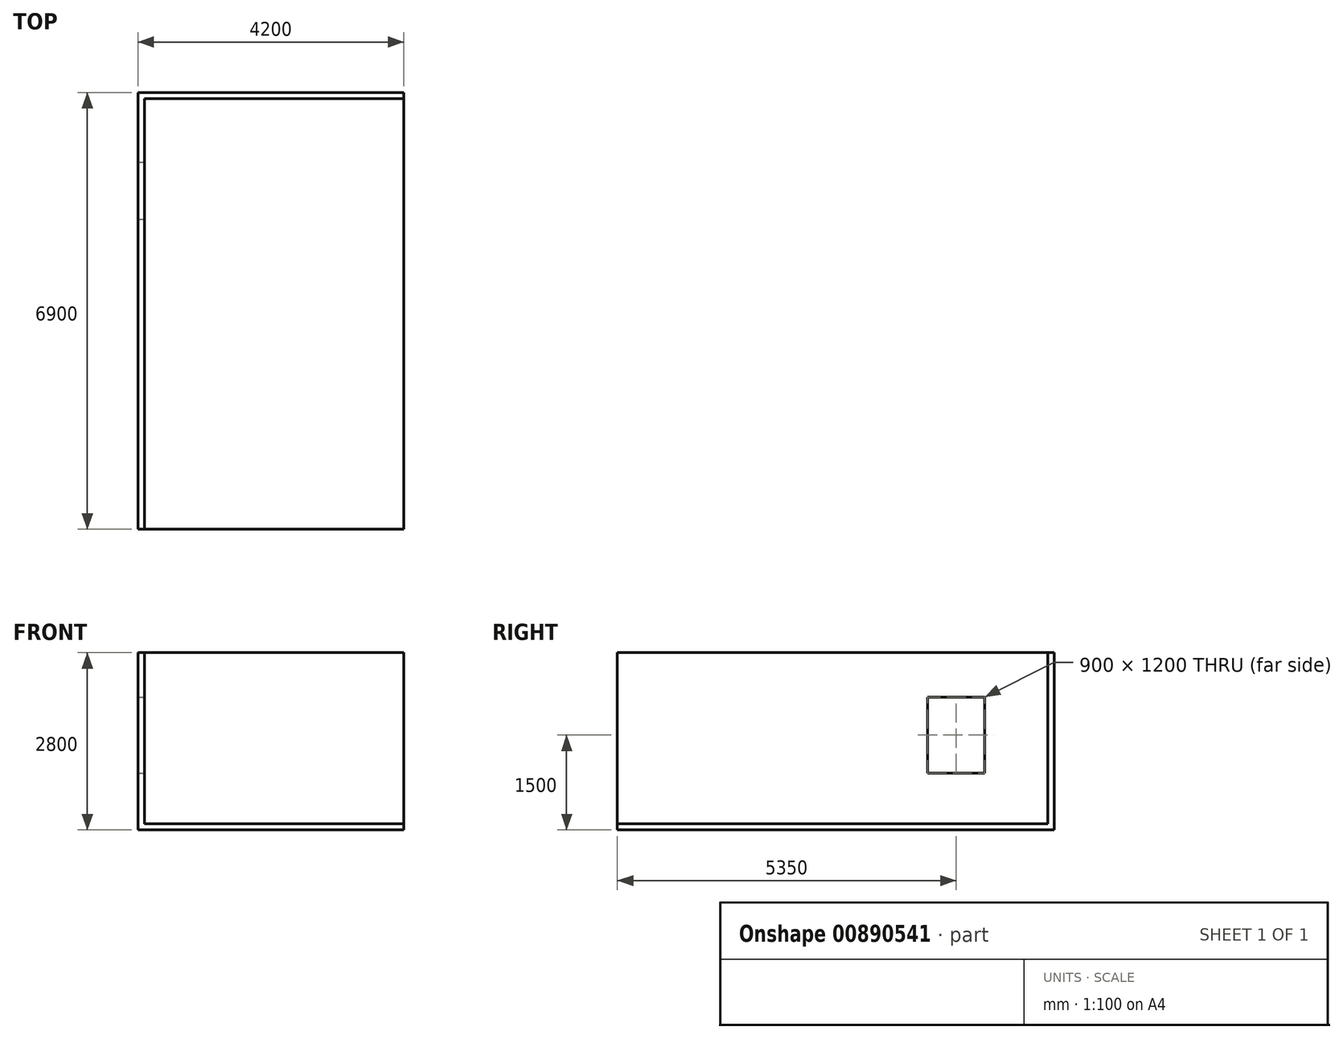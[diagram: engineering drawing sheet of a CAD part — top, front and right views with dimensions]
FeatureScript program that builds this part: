
annotation { "Feature Type Name" : "Feature", "Feature Type Description" : "" }
export const myFeature = defineFeature(function(context is Context, id is Id, definition is map)
    precondition{}
    {
        {
            var Q0;
            Q0=qCreatedBy(makeId("Top.planeOp"),FACE);
            var sketch = newSketch(context, id + "F0", { "sketchPlane" : qUnion([Q0])});
            skLineSegment(sketch, "E0.bottom", {"start": v(2100, 3450) * mm, "end": v(-2100, 3450) * mm});
            skLineSegment(sketch, "E0.top", {"start": v(2100, -3450) * mm, "end": v(-2100, -3450) * mm});
            skLineSegment(sketch, "E0.left", {"start": v(2100, 3450) * mm, "end": v(2100, -3450) * mm});
            skLineSegment(sketch, "E0.right", {"start": v(-2100, 3450) * mm, "end": v(-2100, -3450) * mm});
            skPoint(sketch, "E0.middle", {"position": v(0, 0) * mm});
            skSolve(sketch);
        }
        {
            var Q0;
            Q0=makeQuery(id+"F0.imprint","IMPRINT",FACE,{"disambiguationData":[TD([[makeQuery(id+"F0.imprint","IMPRINT",EDGE,{"derivedFrom":sQuery(id+"F0.wireOp",EDGE,"E0.bottom")}),1.0]])]});
            extrude(context, id + "F1", {"entities" : qUnion([Q0]), "depth" : 2800 * mm, "offsetDistance" : 25 * mm});
        }
        {
            var Q0;
            Q0=makeQuery(id+"F1.opExtrude","CAP_FACE",FACE,{"disambiguationData":[OSD([sQuery(id+"F0.wireOp",EDGE,"E0.bottom"),sQuery(id+"F0.wireOp",EDGE,"E0.top"),sQuery(id+"F0.wireOp",EDGE,"E0.left"),sQuery(id+"F0.wireOp",EDGE,"E0.right")])],"isStart":false});
            var Q1;
            Q1=makeQuery(id+"F1.opExtrude","SWEPT_FACE",FACE,{"disambiguationData":[OSD([sQuery(id+"F0.wireOp",EDGE,"E0.left")])]});
            var Q2;
            Q2=makeQuery(id+"F1.opExtrude","SWEPT_FACE",FACE,{"disambiguationData":[OSD([sQuery(id+"F0.wireOp",EDGE,"E0.top")])]});
            shell(context, id + "F2", {"entities" : qUnion([Q0, Q1, Q2]), "thickness" : 100 * mm});
        }
        {
            var Q0;
            Q0=makeQuery(id+"F2.opShell","OFFSET_FACE",FACE,{"disambiguationData":[OSD([sQuery(id+"F0.wireOp",EDGE,"E0.right")])]});
            var sketch = newSketch(context, id + "F3", { "sketchPlane" : qUnion([Q0])});
            skLineSegment(sketch, "E1.bottom", {"start": v(1450, 2100) * mm, "end": v(2350, 2100) * mm});
            skLineSegment(sketch, "E1.top", {"start": v(1450, 900) * mm, "end": v(2350, 900) * mm});
            skLineSegment(sketch, "E1.left", {"start": v(1450, 2100) * mm, "end": v(1450, 900) * mm});
            skLineSegment(sketch, "E1.right", {"start": v(2350, 2100) * mm, "end": v(2350, 900) * mm});
            skPoint(sketch, "E1.middle", {"position": v(1900, 1500) * mm});
            skSolve(sketch);
        }
        {
            var Q0;
            Q0=makeQuery(id+"F3.imprint","IMPRINT",FACE,{"disambiguationData":[TD([[makeQuery(id+"F3.imprint","IMPRINT",EDGE,{"derivedFrom":sQuery(id+"F3.wireOp",EDGE,"E1.bottom")}),-1.0]])]});
            extrude(context, id + "F4", {"entities" : qUnion([Q0]), "operationType" : NewBodyOperationType.REMOVE, "endBound" : BoundingType.THROUGH_ALL, "oppositeDirection" : true, "depth" : 610 * mm, "offsetDistance" : 25 * mm});
        }
    });
